# Revit family: Mechanical_Stoppers-Exapandable-Champion_Couplings-C1440-NH_Series
name_source: partatom
category: Pipe Fittings
revit_build: Autodesk Revit 2014 (Build: 20130308_1515(x64)
units: mm (PartAtom-declared; Revit-internal decimal feet)

## types (1)
- C1440-NH
    Assembly Code = D2090800
    CW Connection = Yes
    Description = : MIFAB® Series C1440-NH (select model number) expandable mecahnical stoppers. The C1440-NH meets and
exceed the requirements of the ASTM C425 Standard.
    HW Connection = No
    Height = 1.150"
    List Price (Each Piece) = $2.65
    Manufacturer = Champion Couplings
    Material = Rubber-Champion Couplings-Flexible Rubber
    Model = C1440-NH
    Pipe Connection Diameter = 1.500"
    Pipe Size Description = 1 1/2"
    Price = Prices may vary. Please consult Manufacturer Representative for most up-to-date price list.
    Product Documentation Link = http://www.mifab.com
    Product Page URL = http://www.mifab.com
    Standard Listings & Approval = CSA Approved, U.P.C. Approved
    Tick Size = 0.644"
    URL = http://www.mifab.com
    Vent Connection = No
    Warranty Information = 1 Year Warranty
    Waste Connection = No
    Width A = 1.610"
    Width B = 1.950"

## geometry (parser evidence)
native form markers: Sweep x3
no freeform markers — native parametric forms only
